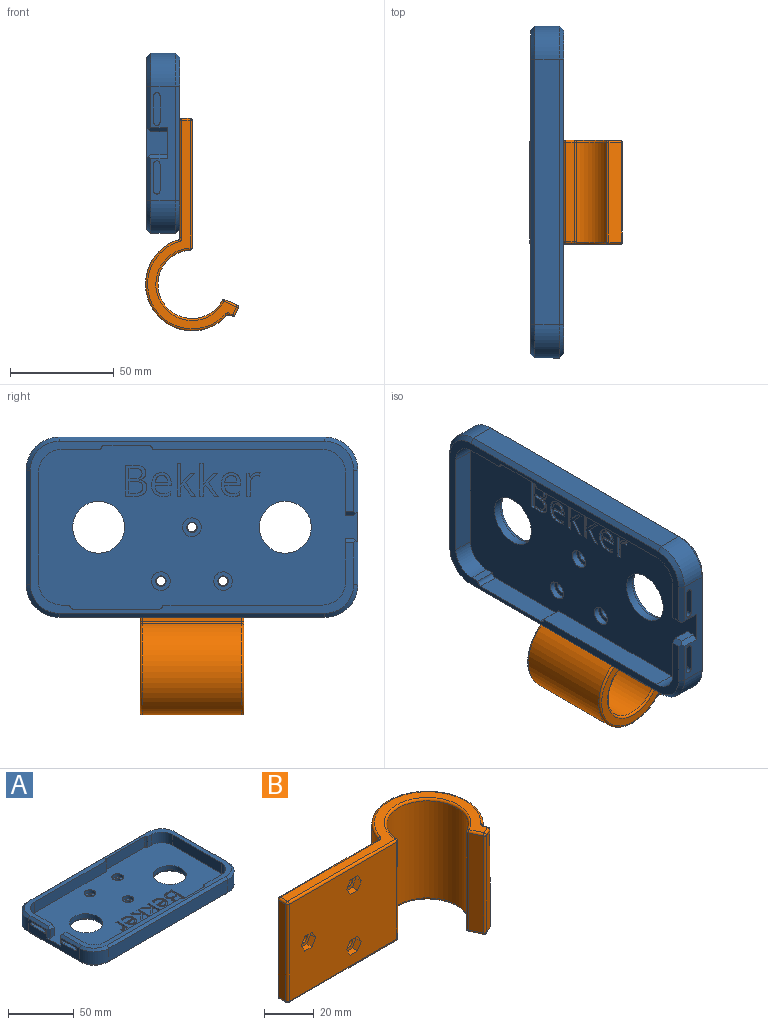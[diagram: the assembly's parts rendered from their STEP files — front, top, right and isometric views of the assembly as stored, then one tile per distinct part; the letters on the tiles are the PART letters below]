
ASSEMBLY  parts=2 mates=3
PART A: 188 faces, bbox 160x87x16 mm
  f0: plane 156x83mm, normal (0,0,1), area 1587.1mm2, adj f1,f3,f4,f5,f14,f15,f16,f17
  f1: plane 21x10mm, normal (1,0,0), area 161.9mm2, adj f0,f6,f18,f174,f178,f184,f185,f186
  f2: plane 55x12mm, normal (-1,0,0), area 447.9mm2, adj f3,f6,f23,f24,f37,f44,f177,f179
  f3: plane 21x2mm, normal (-0.71,0,0.71), area 58mm2, adj f0,f2,f46,f178,f179
  f4: plane 77x10mm, normal (0,-1,0), area 770mm2, adj f0,f6,f20,f172
  f5: plane 82x10mm, normal (0,1,0), area 820mm2, adj f0,f6,f18,f170
  f6: plane 154x79mm, normal (0,0,1), area 9636.2mm2, adj f1,f2,f4,f5,f14,f15,f16,f17
  f7: cylinder r=2.5mm len=5mm, axis (0,0,1), area 47.1mm2, adj f13,f30
  f8: cylinder r=2.5mm len=5mm, axis (0,0,1), area 47.1mm2, adj f13,f28
  f9: cylinder r=2.5mm len=5mm, axis (0,0,1), area 47.1mm2, adj f13,f26
  f10: plane 55x12mm, normal (1,0,0), area 660mm2, adj f22,f25,f34,f43
  f11: plane 128x12mm, normal (0,1,0), area 1536mm2, adj f22,f23,f38,f40
  f12: plane 128x12mm, normal (0,-1,0), area 1536mm2, adj f24,f25,f33,f47
  f13: plane 156x83mm, normal (0,0,-1), area 11399.8mm2, adj f7,f8,f9,f32,f33,f34,f35,f36
  f14: plane 53x10mm, normal (-1,0,0), area 530mm2, adj f0,f6,f19,f21
  f15: plane 10x4mm, normal (0,-1,0), area 40mm2, adj f0,f6,f21,f173
  f16: plane 21x10mm, normal (1,0,0), area 161.9mm2, adj f0,f6,f20,f175,f176,f180,f181,f182
  f17: plane 19x10mm, normal (0,1,0), area 190mm2, adj f0,f6,f19,f171
  f18: cylinder r=11mm len=11mm, axis (0,0,-1), area 172.8mm2, adj f0,f1,f5,f6
  f19: cylinder r=11mm len=11mm, axis (0,0,1), area 172.8mm2, adj f0,f6,f14,f17
  f20: cylinder r=11mm len=11mm, axis (0,0,1), area 172.8mm2, adj f0,f4,f6,f16
  f21: cylinder r=11mm len=11mm, axis (0,0,-1), area 172.8mm2, adj f0,f6,f14,f15
  f22: cylinder r=16mm len=16mm, axis (0,0,1), area 301.6mm2, adj f10,f11,f36,f41
  f23: cylinder r=16mm len=16mm, axis (0,0,-1), area 301.6mm2, adj f2,f11,f39,f42
  f24: cylinder r=16mm len=16mm, axis (0,0,1), area 301.6mm2, adj f2,f12,f35,f46
  f25: cylinder r=16mm len=16mm, axis (0,0,-1), area 301.6mm2, adj f10,f12,f32,f45
  f26: plane 9x9mm, normal (0,0,1), area 44mm2, adj f9,f27
  f27: cylinder r=4.5mm len=9mm, axis (0,0,1), area 84.8mm2, adj f6,f26
  f28: plane 9x9mm, normal (0,0,1), area 44mm2, adj f8,f29
  f29: cylinder r=4.5mm len=9mm, axis (0,0,1), area 84.8mm2, adj f6,f28
  f30: plane 9x9mm, normal (0,0,1), area 44mm2, adj f7,f31
  f31: cylinder r=4.5mm len=9mm, axis (0,0,1), area 84.8mm2, adj f6,f30
  f32: cone r=14mm half-angle=45deg, axis (0,0,1), area 66.6mm2, adj f13,f25,f33,f34
  f33: plane 128x2mm, normal (0,-0.71,-0.71), area 362mm2, adj f12,f13,f32,f35
  f34: plane 55x2mm, normal (0.71,0,-0.71), area 155.6mm2, adj f10,f13,f32,f36
  f35: cone r=14mm half-angle=45deg, axis (0,0,1), area 66.6mm2, adj f13,f24,f33,f37
  f36: cone r=14mm half-angle=45deg, axis (0,0,1), area 66.6mm2, adj f13,f22,f34,f38
  f37: plane 55x2mm, normal (-0.71,0,-0.71), area 155.6mm2, adj f2,f13,f35,f39
  f38: plane 128x2mm, normal (0,0.71,-0.71), area 362mm2, adj f11,f13,f36,f39
  f39: cone r=14mm half-angle=45deg, axis (0,0,1), area 66.6mm2, adj f13,f23,f37,f38
  f40: plane 128x2mm, normal (0,0.71,0.71), area 362mm2, adj f0,f11,f41,f42
  f41: cone r=14mm half-angle=45deg, axis (0,0,-1), area 66.6mm2, adj f0,f22,f40,f43
  f42: cone r=14mm half-angle=45deg, axis (0,0,-1), area 66.6mm2, adj f0,f23,f40,f44
  f43: plane 55x2mm, normal (0.71,0,0.71), area 155.6mm2, adj f0,f10,f41,f45
  f44: plane 21x2mm, normal (-0.71,0,0.71), area 58mm2, adj f0,f2,f42,f176,f177
  f45: cone r=14mm half-angle=45deg, axis (0,0,-1), area 66.6mm2, adj f0,f25,f43,f47
  f46: cone r=14mm half-angle=45deg, axis (0,0,-1), area 66.6mm2, adj f0,f3,f24,f47
  f47: plane 128x2mm, normal (0,-0.71,0.71), area 362mm2, adj f0,f12,f45,f46
  f48: cylinder r=12.5mm len=25mm, axis (0,0,1), area 314.2mm2, adj f6,f51
  f49: cylinder r=12.5mm len=25mm, axis (0,0,1), area 314.2mm2, adj f6,f50
  f50: torus R=14.5mm, axis (0,0,1), area 261.1mm2, adj f13,f49
  f51: torus R=14.5mm, axis (0,0,1), area 261.1mm2, adj f13,f48
  f52: extruded ~1.63x1.33mm, area 2.1mm2, adj f6,f53,f66,f67
  f53: plane 1x0.08mm, normal (0,1,0), area 0.1mm2, adj f6,f52,f54,f67
  f54: extruded ~1.73x1mm, area 1.7mm2, adj f6,f53,f55,f67
  f55: plane 8.4x1mm, normal (1,0,0), area 8.4mm2, adj f6,f54,f56,f67
  f56: plane 1.67x1mm, normal (0,1,0), area 1.7mm2, adj f6,f55,f57,f67
  f57: plane 15.83x1mm, normal (-1,0,0), area 15.8mm2, adj f6,f56,f58,f67
  f58: plane 1.67x1mm, normal (0,-1,0), area 1.7mm2, adj f6,f57,f59,f67
  f59: plane 4.17x1mm, normal (1,0,0), area 4.2mm2, adj f6,f58,f60,f67
  f60: plane 1.27x1.1mm, normal (0.65,-0.76,0), area 1.7mm2, adj f6,f59,f61,f67
  f61: plane 5.27x3.94mm, normal (-0.8,-0.6,0), area 6.6mm2, adj f6,f60,f62,f67
  f62: plane 2.04x1mm, normal (0,-1,0), area 2mm2, adj f6,f61,f63,f67
  f63: plane 6.4x4.83mm, normal (0.8,0.6,0), area 8mm2, adj f6,f62,f64,f67
  f64: plane 4.75x4.52mm, normal (0.72,-0.69,0), area 6.6mm2, adj f6,f63,f65,f67
  f65: plane 2.01x1mm, normal (0,1,0), area 2mm2, adj f6,f64,f66,f67
  f66: plane 3.82x3.6mm, normal (-0.73,0.69,0), area 5.2mm2, adj f6,f52,f65,f67
  f67: plane 15.83x8.92mm, normal (0,0,1), area 50.2mm2, adj f52,f53,f54,f55,f56,f57,f58,f59
  f68: extruded ~2.14x1mm, area 2.4mm2, adj f69,f86,f87,f165
  f69: extruded ~2.04x1mm, area 2.3mm2, adj f68,f70,f87,f165
  f70: extruded ~2.44x1mm, area 2.6mm2, adj f69,f71,f87,f165
  f71: plane 5.83x1mm, normal (0,1,0), area 5.8mm2, adj f70,f86,f87,f165
  f72: extruded ~3.9x1.51mm, area 4.3mm2, adj f6,f73,f85,f87
  f73: extruded ~1.93x1mm, area 1.9mm2, adj f6,f72,f74,f87
  f74: extruded ~1.69x1mm, area 1.8mm2, adj f6,f73,f75,f87
  f75: plane 1.51x1mm, normal (1,0,0), area 1.5mm2, adj f6,f74,f76,f87
  f76: extruded ~3.56x1mm, area 3.7mm2, adj f6,f75,f77,f87
  f77: extruded ~2.65x1.02mm, area 2.9mm2, adj f6,f76,f78,f87
  f78: extruded ~2.98x1mm, area 3.2mm2, adj f6,f77,f79,f87
  f79: plane 7.68x1mm, normal (0,-1,0), area 7.7mm2, adj f6,f78,f80,f87
  f80: plane 1.07x1mm, normal (1,0,0), area 1.1mm2, adj f6,f79,f81,f87
  f81: extruded ~3.64x1.22mm, area 3.9mm2, adj f6,f80,f82,f87
  f82: extruded ~3.31x1.38mm, area 3.7mm2, adj f6,f81,f83,f87
  f83: extruded ~3.57x1.59mm, area 4mm2, adj f6,f82,f84,f87
  f84: extruded ~4.29x1.33mm, area 4.6mm2, adj f6,f83,f85,f87
  f85: extruded ~4.18x1.43mm, area 4.5mm2, adj f6,f72,f84,f87
  f86: extruded ~2.42x1mm, area 2.6mm2, adj f68,f71,f87,f165
  f87: plane 11.56x9.43mm, normal (0,0,1), area 49.6mm2, adj f68,f69,f70,f71,f72,f73,f74,f75
  f88: extruded ~2.14x1mm, area 2.4mm2, adj f89,f106,f107,f166
  f89: extruded ~2.04x1mm, area 2.3mm2, adj f88,f90,f107,f166
  f90: extruded ~2.44x1mm, area 2.6mm2, adj f89,f91,f107,f166
  f91: plane 5.83x1mm, normal (0,1,0), area 5.8mm2, adj f90,f106,f107,f166
  f92: extruded ~3.9x1.51mm, area 4.3mm2, adj f6,f93,f105,f107
  f93: extruded ~1.93x1mm, area 1.9mm2, adj f6,f92,f94,f107
  f94: extruded ~1.69x1mm, area 1.8mm2, adj f6,f93,f95,f107
  f95: plane 1.51x1mm, normal (1,0,0), area 1.5mm2, adj f6,f94,f96,f107
  f96: extruded ~3.56x1mm, area 3.7mm2, adj f6,f95,f97,f107
  f97: extruded ~2.65x1.02mm, area 2.9mm2, adj f6,f96,f98,f107
  f98: extruded ~2.98x1mm, area 3.2mm2, adj f6,f97,f99,f107
  f99: plane 7.68x1mm, normal (0,-1,0), area 7.7mm2, adj f6,f98,f100,f107
  f100: plane 1.07x1mm, normal (1,0,0), area 1.1mm2, adj f6,f99,f101,f107
  f101: extruded ~3.64x1.22mm, area 3.9mm2, adj f6,f100,f102,f107
  f102: extruded ~3.31x1.38mm, area 3.7mm2, adj f6,f101,f103,f107
  f103: extruded ~3.57x1.59mm, area 4mm2, adj f6,f102,f104,f107
  f104: extruded ~4.29x1.33mm, area 4.6mm2, adj f6,f103,f105,f107
  f105: extruded ~4.18x1.43mm, area 4.5mm2, adj f6,f92,f104,f107
  f106: extruded ~2.42x1mm, area 2.6mm2, adj f88,f91,f107,f166
  f107: plane 11.56x9.43mm, normal (0,0,1), area 49.6mm2, adj f88,f89,f90,f91,f92,f93,f94,f95
  f108: extruded ~1.33x1mm, area 1.3mm2, adj f6,f109,f120,f121
  f109: extruded ~1.92x1mm, area 2mm2, adj f6,f108,f110,f121
  f110: extruded ~1.68x1.49mm, area 2.3mm2, adj f6,f109,f111,f121
  f111: plane 1x0.08mm, normal (0,1,0), area 0.1mm2, adj f6,f110,f112,f121
  f112: plane 2.06x1mm, normal (1,0.09,0), area 2.1mm2, adj f6,f111,f113,f121
  f113: plane 1.39x1mm, normal (0,1,0), area 1.4mm2, adj f6,f112,f114,f121
  f114: plane 11.15x1mm, normal (-1,0,0), area 11.1mm2, adj f6,f113,f115,f121
  f115: plane 1.69x1mm, normal (0,-1,0), area 1.7mm2, adj f6,f114,f116,f121
  f116: plane 5.98x1mm, normal (1,0,0), area 6mm2, adj f6,f115,f117,f121
  f117: extruded ~2.74x1mm, area 3mm2, adj f6,f116,f118,f121
  f118: extruded ~2.31x1.1mm, area 2.6mm2, adj f6,f117,f119,f121
  f119: extruded ~1.22x1mm, area 1.2mm2, adj f6,f118,f120,f121
  f120: plane 1.57x1mm, normal (0.99,-0.15,0), area 1.6mm2, adj f6,f108,f119,f121
  f121: plane 11.35x6.42mm, normal (0,0,1), area 25.9mm2, adj f108,f109,f110,f111,f112,f113,f114,f115
  f122: extruded ~1.63x1.33mm, area 2.1mm2, adj f6,f123,f136,f137
  f123: plane 1x0.08mm, normal (0,1,0), area 0.1mm2, adj f6,f122,f124,f137
  f124: extruded ~1.73x1mm, area 1.7mm2, adj f6,f123,f125,f137
  f125: plane 8.4x1mm, normal (1,0,0), area 8.4mm2, adj f6,f124,f126,f137
  f126: plane 1.67x1mm, normal (0,1,0), area 1.7mm2, adj f6,f125,f127,f137
  f127: plane 15.83x1mm, normal (-1,0,0), area 15.8mm2, adj f6,f126,f128,f137
  f128: plane 1.67x1mm, normal (0,-1,0), area 1.7mm2, adj f6,f127,f129,f137
  f129: plane 4.17x1mm, normal (1,0,0), area 4.2mm2, adj f6,f128,f130,f137
  f130: plane 1.27x1.1mm, normal (0.65,-0.76,0), area 1.7mm2, adj f6,f129,f131,f137
  f131: plane 5.27x3.94mm, normal (-0.8,-0.6,0), area 6.6mm2, adj f6,f130,f132,f137
  f132: plane 2.04x1mm, normal (0,-1,0), area 2mm2, adj f6,f131,f133,f137
  f133: plane 6.4x4.83mm, normal (0.8,0.6,0), area 8mm2, adj f6,f132,f134,f137
  f134: plane 4.75x4.52mm, normal (0.72,-0.69,0), area 6.6mm2, adj f6,f133,f135,f137
  f135: plane 2.01x1mm, normal (0,1,0), area 2mm2, adj f6,f134,f136,f137
  f136: plane 3.82x3.6mm, normal (-0.73,0.69,0), area 5.2mm2, adj f6,f122,f135,f137
  f137: plane 15.83x8.92mm, normal (0,0,1), area 50.2mm2, adj f122,f123,f124,f125,f126,f127,f128,f129
  f138: plane 5.57x1mm, normal (1,0,0), area 5.6mm2, adj f139,f162,f163,f167
  f139: plane 2.96x1mm, normal (0,-1,0), area 3mm2, adj f138,f140,f163,f167
  f140: extruded ~2.83x1mm, area 2.9mm2, adj f139,f141,f163,f167
  f141: extruded ~2.03x1mm, area 2.3mm2, adj f140,f142,f163,f167
  f142: extruded ~2.18x1mm, area 2.5mm2, adj f141,f143,f163,f167
  f143: extruded ~2.71x1mm, area 2.8mm2, adj f142,f162,f163,f167
  f144: plane 2.85x1mm, normal (0,1,0), area 2.8mm2, adj f145,f160,f163,f164
  f145: plane 4.87x1mm, normal (1,0,0), area 4.9mm2, adj f144,f146,f163,f164
  f146: plane 2.55x1mm, normal (0,-1,0), area 2.5mm2, adj f145,f147,f163,f164
  f147: extruded ~2.85x1mm, area 2.9mm2, adj f146,f148,f163,f164
  f148: extruded ~1.81x1mm, area 2.1mm2, adj f147,f149,f163,f164
  f149: extruded ~1.94x1mm, area 2.2mm2, adj f148,f160,f163,f164
  f150: plane 4.2x1mm, normal (0,1,0), area 4.2mm2, adj f6,f151,f161,f163
  f151: plane 14.87x1mm, normal (-1,0,0), area 14.9mm2, adj f6,f150,f152,f163
  f152: plane 5.19x1mm, normal (0,-1,0), area 5.2mm2, adj f6,f151,f153,f163
  f153: extruded ~3.77x1.12mm, area 4mm2, adj f6,f152,f154,f163
  f154: extruded ~3.11x1.35mm, area 3.5mm2, adj f6,f153,f155,f163
  f155: extruded ~3.56x3.39mm, area 5.4mm2, adj f6,f154,f156,f163
  f156: plane 1x0.1mm, normal (1,0,0), area 0.1mm2, adj f6,f155,f157,f163
  f157: extruded ~2.15x1.11mm, area 2.5mm2, adj f6,f156,f158,f163
  f158: extruded ~2.18x1mm, area 2.4mm2, adj f6,f157,f159,f163
  f159: extruded ~2.8x1.32mm, area 3.2mm2, adj f6,f158,f161,f163
  f160: extruded ~2.64x1mm, area 2.7mm2, adj f144,f149,f163,f164
  f161: extruded ~4.28x1mm, area 4.4mm2, adj f6,f150,f159,f163
  f162: plane 3.11x1mm, normal (0,1,0), area 3.1mm2, adj f138,f143,f163,f167
  f163: plane 14.87x10.31mm, normal (0,0,1), area 75.4mm2, adj f138,f139,f140,f141,f142,f143,f144,f145
  f164: plane 6.29x4.87mm, normal (0,0,1), area 28mm2, adj f144,f145,f146,f147,f148,f149,f160
  f165: plane 5.83x3.29mm, normal (0,0,1), area 15.5mm2, adj f68,f69,f70,f71,f86
  f166: plane 5.83x3.29mm, normal (0,0,1), area 15.5mm2, adj f88,f89,f90,f91,f106
  f167: plane 6.73x5.57mm, normal (0,0,1), area 34.1mm2, adj f138,f139,f140,f141,f142,f143,f162
  f168: plane 21x10mm, normal (0,1,0), area 210mm2, adj f0,f6,f170,f171
  f169: plane 41x10mm, normal (0,-1,0), area 410mm2, adj f0,f6,f172,f173
  f170: cylinder r=2mm len=10mm, axis (0,0,1), area 31.4mm2, adj f0,f5,f6,f168
  f171: cylinder r=2mm len=10mm, axis (0,0,-1), area 31.4mm2, adj f0,f6,f17,f168
  f172: cylinder r=2mm len=10mm, axis (0,0,-1), area 31.4mm2, adj f0,f4,f6,f169
  f173: cylinder r=2mm len=10mm, axis (0,0,1), area 31.4mm2, adj f0,f6,f15,f169
  f174: plane 8x4mm, normal (0,1,0), area 32mm2, adj f1,f6,f178,f179
  f175: plane 8x4mm, normal (0,-1,0), area 32mm2, adj f6,f16,f176,f177
  f176: plane 5x2mm, normal (0,-0.71,0.71), area 12.7mm2, adj f0,f16,f44,f175,f177
  f177: plane 9x2mm, normal (-0.71,-0.71,0), area 24mm2, adj f2,f6,f44,f175,f176
  f178: plane 5x2mm, normal (0,0.71,0.71), area 12.7mm2, adj f0,f1,f3,f174,f179
  f179: plane 9x2mm, normal (-0.71,0.71,0), area 24mm2, adj f2,f3,f6,f174,f178
  f180: plane 13x6mm, normal (0,0,-1), area 78mm2, adj f2,f16,f181,f183
  f181: cylinder r=1.5mm len=6mm, axis (-1,0,0), area 28.3mm2, adj f2,f16,f180,f182
  f182: plane 13x6mm, normal (0,0,1), area 78mm2, adj f2,f16,f181,f183
  f183: cylinder r=1.5mm len=6mm, axis (-1,0,0), area 28.3mm2, adj f2,f16,f180,f182
  f184: plane 13x6mm, normal (0,0,-1), area 78mm2, adj f1,f2,f185,f187
  f185: cylinder r=1.5mm len=6mm, axis (-1,0,0), area 28.3mm2, adj f1,f2,f184,f186
  f186: plane 13x6mm, normal (0,0,1), area 78mm2, adj f1,f2,f185,f187
  f187: cylinder r=1.5mm len=6mm, axis (-1,0,0), area 28.3mm2, adj f1,f2,f184,f186
PART B: 74 faces, bbox 104.4x46.7x50 mm
  f0: plane 100.5x42.83mm, normal (0,0,1), area 568.3mm2, adj f35,f37,f38,f44,f47,f48,f57,f58
  f1: cylinder r=2.25mm len=4.5mm, axis (0,1,0), area 42.4mm2, adj f9,f27
  f2: cylinder r=2.25mm len=4.5mm, axis (0,1,0), area 42.4mm2, adj f9,f20
  f3: cylinder r=2.25mm len=4.5mm, axis (0,1,0), area 42.4mm2, adj f9,f13
  f4: cylinder r=16.5mm len=48mm, axis (0,0,-1), area 3296.1mm2, adj f62,f67,f70,f73
  f5: plane 48x5.92mm, normal (-0.91,-0.42,0), area 313.4mm2, adj f59,f68,f69,f73
  f6: plane 48x3.63mm, normal (0.42,-0.91,0), area 192mm2, adj f49,f58,f59,f60
  f7: plane 48x1.42mm, normal (0.91,0.42,0), area 75.2mm2, adj f39,f48,f49,f50
  f8: cylinder r=22.5mm len=48mm, axis (0,0,-1), area 3964.8mm2, adj f34,f38,f39,f40
  f9: plane 56.57x48mm, normal (0,1,0), area 2667.5mm2, adj f1,f2,f3,f34,f37,f41,f42
  f10: plane 48x4mm, normal (-1,0,0), area 192mm2, adj f42,f47,f51,f52
  f11: plane 61.53x48mm, normal (0,-1,0), area 2818.7mm2, adj f14,f15,f16,f17,f18,f19,f21,f22
  f12: plane 100.5x42.83mm, normal (0,0,-1), area 568.3mm2, adj f36,f40,f41,f45,f50,f51,f60,f61
  f13: plane 8.31x7.2mm, normal (0,-1,0), area 29mm2, adj f3,f14,f15,f16,f17,f18,f19
  f14: plane 3.6x3mm, normal (0.87,0,0.5), area 12.5mm2, adj f11,f13,f15,f19
  f15: plane 4.16x3mm, normal (0,0,1), area 12.5mm2, adj f11,f13,f14,f16
  f16: plane 3.6x3mm, normal (-0.87,0,0.5), area 12.5mm2, adj f11,f13,f15,f17
  f17: plane 3.6x3mm, normal (-0.87,0,-0.5), area 12.5mm2, adj f11,f13,f16,f18
  f18: plane 4.16x3mm, normal (0,0,-1), area 12.5mm2, adj f11,f13,f17,f19
  f19: plane 3.6x3mm, normal (0.87,0,-0.5), area 12.5mm2, adj f11,f13,f14,f18
  f20: plane 8.31x7.2mm, normal (0,-1,0), area 29mm2, adj f2,f21,f22,f23,f24,f25,f26
  f21: plane 3.6x3mm, normal (0.87,0,0.5), area 12.5mm2, adj f11,f20,f22,f26
  f22: plane 4.16x3mm, normal (0,0,1), area 12.5mm2, adj f11,f20,f21,f23
  f23: plane 3.6x3mm, normal (-0.87,0,0.5), area 12.5mm2, adj f11,f20,f22,f24
  f24: plane 3.6x3mm, normal (-0.87,0,-0.5), area 12.5mm2, adj f11,f20,f23,f25
  f25: plane 4.16x3mm, normal (0,0,-1), area 12.5mm2, adj f11,f20,f24,f26
  f26: plane 3.6x3mm, normal (0.87,0,-0.5), area 12.5mm2, adj f11,f20,f21,f25
  f27: plane 8.31x7.2mm, normal (0,-1,0), area 29mm2, adj f1,f28,f29,f30,f31,f32,f33
  f28: plane 3.6x3mm, normal (0.87,0,0.5), area 12.5mm2, adj f11,f27,f29,f33
  f29: plane 4.16x3mm, normal (0,0,1), area 12.5mm2, adj f11,f27,f28,f30
  f30: plane 3.6x3mm, normal (-0.87,0,0.5), area 12.5mm2, adj f11,f27,f29,f31
  f31: plane 3.6x3mm, normal (-0.87,0,-0.5), area 12.5mm2, adj f11,f27,f30,f32
  f32: plane 4.16x3mm, normal (0,0,-1), area 12.5mm2, adj f11,f27,f31,f33
  f33: plane 3.6x3mm, normal (0.87,0,-0.5), area 12.5mm2, adj f11,f27,f28,f32
  f34: cylinder r=1mm len=48mm, axis (0,0,-1), area 60.9mm2, adj f8,f9,f35,f36
  f35: torus R=2mm, axis (0,0,1), area 2.7mm2, adj f0,f34,f37,f38
  f36: torus R=2mm, axis (0,0,1), area 2.7mm2, adj f12,f34,f40,f41
  f37: cylinder r=1mm len=56.57mm, axis (1,0,0), area 88.9mm2, adj f0,f9,f35,f43
  f38: torus R=21.5mm, axis (0,0,1), area 127.7mm2, adj f0,f8,f35,f44
  f39: cylinder r=1mm len=48mm, axis (0,0,-1), area 60.9mm2, adj f7,f8,f44,f45
  f40: torus R=21.5mm, axis (0,0,1), area 127.7mm2, adj f8,f12,f36,f45
  f41: cylinder r=1mm len=56.57mm, axis (-1,0,0), area 88.9mm2, adj f9,f12,f36,f46
  f42: cylinder r=1mm len=48mm, axis (0,0,-1), area 75.4mm2, adj f9,f10,f43,f46
  f43: sphere r=1mm, area 1.6mm2, adj f37,f42,f47
  f44: torus R=2mm, axis (0,0,1), area 2.7mm2, adj f0,f38,f39,f48
  f45: torus R=2mm, axis (0,0,1), area 2.7mm2, adj f12,f39,f40,f50
  f46: sphere r=1mm, area 1.6mm2, adj f41,f42,f51
  f47: cylinder r=1mm len=4mm, axis (0,1,0), area 6.3mm2, adj f0,f10,f43,f53
  f48: cylinder r=1mm len=1.84mm, axis (0.42,-0.91,0), area 2.5mm2, adj f0,f7,f44,f54
  f49: cylinder r=1mm len=48mm, axis (0,0,-1), area 75.4mm2, adj f6,f7,f54,f55
  f50: cylinder r=1mm len=1.84mm, axis (-0.42,0.91,0), area 2.5mm2, adj f7,f12,f45,f55
  f51: cylinder r=1mm len=4mm, axis (0,-1,0), area 6.3mm2, adj f10,f12,f46,f56
  f52: cylinder r=1mm len=48mm, axis (0,0,-1), area 75.4mm2, adj f10,f11,f53,f56
  f53: sphere r=1mm, area 1.6mm2, adj f47,f52,f57
  f54: sphere r=1mm, area 1.6mm2, adj f48,f49,f58
  f55: sphere r=1mm, area 1.6mm2, adj f49,f50,f60
  f56: sphere r=1mm, area 1.6mm2, adj f51,f52,f61
  f57: cylinder r=1mm len=61.53mm, axis (-1,0,0), area 96.6mm2, adj f0,f11,f53,f63
  f58: cylinder r=1mm len=4.05mm, axis (-0.91,-0.42,0), area 6.3mm2, adj f0,f6,f54,f64
  f59: cylinder r=1mm len=48mm, axis (0,0,-1), area 75.4mm2, adj f5,f6,f64,f65
  f60: cylinder r=1mm len=4.05mm, axis (0.91,0.42,0), area 6.3mm2, adj f6,f12,f55,f65
  f61: cylinder r=1mm len=61.53mm, axis (1,0,0), area 96.6mm2, adj f11,f12,f56,f66
  f62: cylinder r=1mm len=48mm, axis (0,0,-1), area 72.7mm2, adj f4,f11,f63,f66
  f63: sphere r=1mm, area 1.5mm2, adj f57,f62,f67
  f64: sphere r=1mm, area 1.6mm2, adj f58,f59,f68
  f65: sphere r=1mm, area 1.6mm2, adj f59,f60,f69
  f66: sphere r=1mm, area 1.5mm2, adj f61,f62,f70
  f67: torus R=17.5mm, axis (0,0,1), area 110.2mm2, adj f0,f4,f63,f71
  f68: cylinder r=1mm len=6.34mm, axis (-0.42,0.91,0), area 10.3mm2, adj f0,f5,f64,f71
  f69: cylinder r=1mm len=6.34mm, axis (0.42,-0.91,0), area 10.3mm2, adj f5,f12,f65,f72
  f70: torus R=17.5mm, axis (0,0,1), area 110.2mm2, adj f4,f12,f66,f72
  f71: sphere r=1mm, area 1.5mm2, adj f67,f68,f73
  f72: sphere r=1mm, area 1.5mm2, adj f69,f70,f73
  f73: cylinder r=1mm len=48mm, axis (0,0,-1), area 72.7mm2, adj f4,f5,f71,f72
PLACE A rot(axis=(-0.58,-0.58,0.58),120deg) t=(6,0,0)mm
PLACE B rot(axis=(-0.58,0.58,0.58),120deg) t=(12,0,-68)mm
MATE parallel A.f10 <-> B.f0  axis (0,1,0) through (4,80,0)mm
MATE revolute B.f2 <-> A.f9  axis (-1,0,0) through (6,0,0)mm
MATE cylindrical B.f2 <-> A.f9  axis (1,0,0) through (9,0,0)mm
